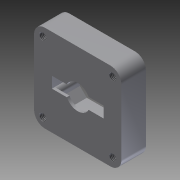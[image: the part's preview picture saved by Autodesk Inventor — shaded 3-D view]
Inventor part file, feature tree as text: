
AUTODESK INVENTOR PART (.ipt)
format: ipt  version: 2012 (Build 160160000, 160)  size: 173,568 bytes
history: native  units: in
note: dims shown in document units (in); Inventor stores cm internally (conversion verified against a paired STEP export)
features: thread x4, extrude x2, fillet x2, hole x2, sketch x1
ambient origin geometry x8: Origin, YZ Plane, XZ Plane, XY Plane, X Axis, Y Axis, Z Axis, Center Point
bodies: Solid1 (feature_tree)
feature tree (11):
  sketch  "Sketch1"  dims[d0=0.9449in d1=0.4724in d2=1.0236in d3=0.5118in d4=0.0787in d5=0.2559in d6=0.128in d7=0.0787in d8=0.5625in d9=2.0in d10=1.0in d11=2.0in d12=1.0in d13=0.1181in d14=0.3937in d15=0.1575in d16=0.1575in d17=0.1575in d18=0.1575in d19=0.1575in d20=0.2in d21=0.2in d22=0.2in d23=0.2in d24=0.5in d25=0.0in d26=0.125in d27=0.164in d28=0.75in d29=0.27in d30=0.2in d31=0.5635in d32=1.0in d33=0.8108in d34=1.6in d35=1.6in d36=1.0in d37=0.0in d38=1.0in d39=0.0in d40=1.0in d41=0.0in d42=1.0in d43=0.0in d44=0.0625in d45=0.0in d46=0.164in d47=0.75in d48=0.375in d49=0.25in d50=0.5635in d51=1.0in d52=0.8108in d53=0.25in]
  extrude  "Extrusion1"  Depth=0.4724in
  fillet  "Fillet1"  Radius=1.0236in
  extrude  "Extrusion2"  Depth=0.5118in
  hole  "Hole1"  [1 undecoded]
  thread  "Thread1"  [1 undecoded]
  thread  "Thread2"  [1 undecoded]
  thread  "Thread3"  [1 undecoded]
  thread  "Thread4"  [1 undecoded]
  hole  "Hole2"  [1 undecoded]
  fillet  "Fillet2"  Radius=1.0in
note: 6 required parameter values undecoded (feature->parameter linkage not recoverable at this tier; creation-order binding heuristic only, values carry confidence <= 0.55)
